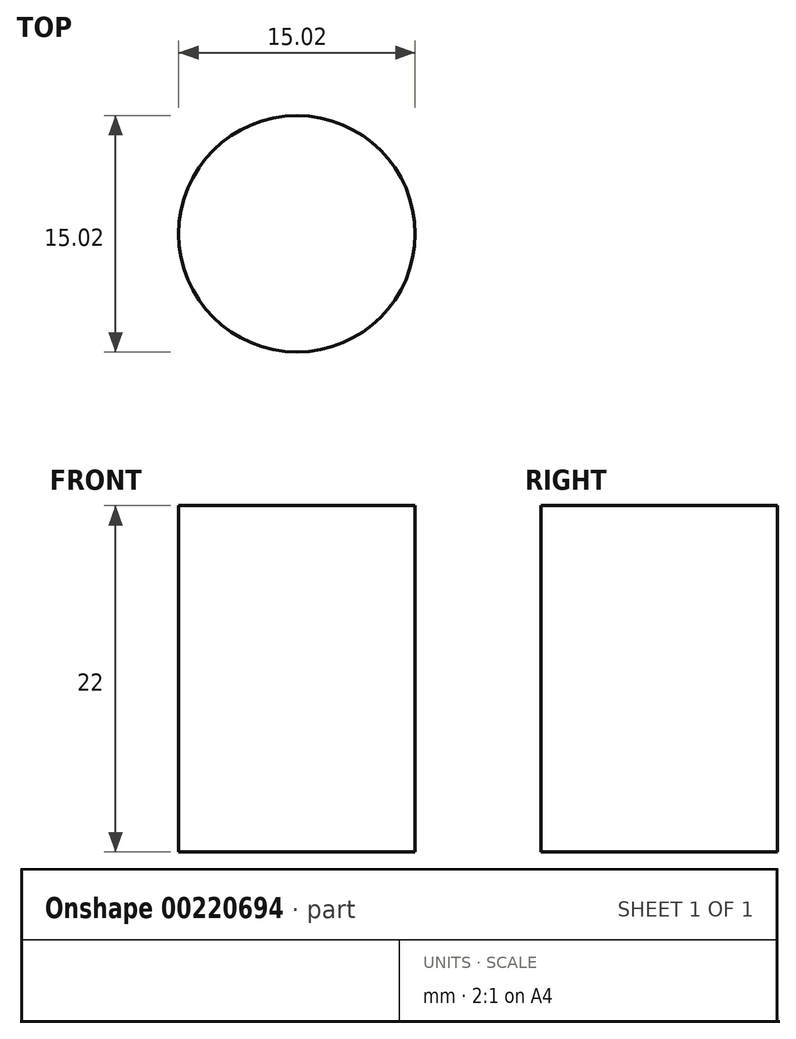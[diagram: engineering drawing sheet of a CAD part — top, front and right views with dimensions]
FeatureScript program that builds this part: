
annotation { "Feature Type Name" : "Feature", "Feature Type Description" : "" }
export const myFeature = defineFeature(function(context is Context, id is Id, definition is map)
    precondition{}
    {
        {
            var Q0;
            Q0=qCreatedBy(makeId("Front.planeOp"),FACE);
            var sketch = newSketch(context, id + "F0", { "sketchPlane" : qUnion([Q0])});
            skLineSegment(sketch, "E0.bottom", {"start": v(0, 0) * mm, "end": v(-7.5, 0) * mm});
            skLineSegment(sketch, "E0.top", {"start": v(0, -22) * mm, "end": v(-7.5, -22) * mm});
            skLineSegment(sketch, "E0.left", {"start": v(0, 0) * mm, "end": v(0, -22) * mm});
            skLineSegment(sketch, "E0.right", {"start": v(-7.5, 0) * mm, "end": v(-7.5, -22) * mm});
            skLineSegment(sketch, "E1.bottom", {"start": v(0, -22) * mm, "end": v(-6.35, -22) * mm});
            skLineSegment(sketch, "E1.top", {"start": v(0, -50.57) * mm, "end": v(-6.35, -50.57) * mm});
            skLineSegment(sketch, "E1.left", {"start": v(0, -22) * mm, "end": v(0, -50.57) * mm});
            skLineSegment(sketch, "E1.right", {"start": v(-6.35, -22) * mm, "end": v(-6.35, -50.57) * mm});
            skLineSegment(sketch, "E2.bottom", {"start": v(0, 0) * mm, "end": v(-3.17, 0) * mm});
            skLineSegment(sketch, "E2.top", {"start": v(0, 10.31) * mm, "end": v(-3.18, 10.31) * mm});
            skLineSegment(sketch, "E2.left", {"start": v(0, 0) * mm, "end": v(0, 10.31) * mm});
            skLineSegment(sketch, "E2.right", {"start": v(-3.18, 0) * mm, "end": v(-3.18, 10.31) * mm});
            skSolve(sketch);
        }
        {
            var Q0;
            Q0=makeQuery(id+"F0.imprint","IMPRINT",FACE,{"disambiguationData":[TD([[makeQuery(id+"F0.imprint","IMPRINT",EDGE,{"derivedFrom":sQuery(id+"F0.wireOp",EDGE,"E2.bottom")}),-1.0]])]});
            var Q1;
            Q1=makeQuery(id+"F0.imprint","IMPRINT",FACE,{"disambiguationData":[TD([[makeQuery(id+"F0.imprint","IMPRINT",EDGE,{"derivedFrom":sQuery(id+"F0.wireOp",EDGE,"E0.bottom")}),1.0]])]});
            var Q2;
            Q2=makeQuery(id+"F0.imprint","IMPRINT",FACE,{"disambiguationData":[TD([[makeQuery(id+"F0.imprint","IMPRINT",EDGE,{"derivedFrom":sQuery(id+"F0.wireOp",EDGE,"E1.bottom")}),1.0]])]});
            var Q3;
            Q3=sQuery(id+"F0.wireOp",EDGE,"E2.left");
            revolve(context, id + "F1", {"entities" : qUnion([Q0, Q1, Q2]), "axis" : qUnion([Q3]), "revolveType" : RevolveType.FULL});
        }
    });
